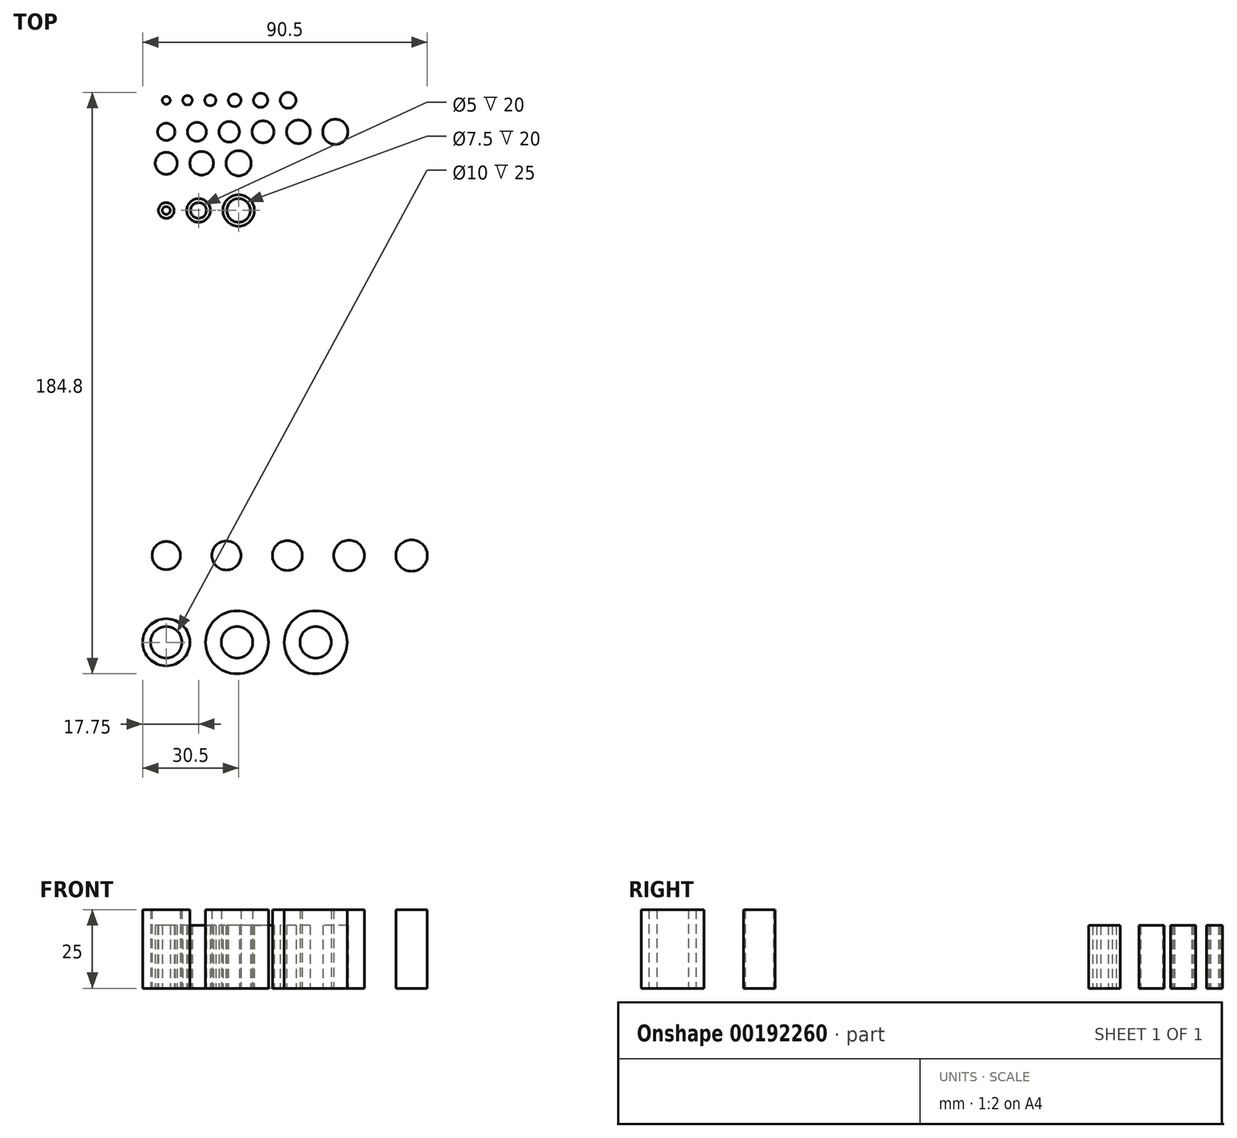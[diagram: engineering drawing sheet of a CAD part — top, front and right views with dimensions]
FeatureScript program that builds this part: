
annotation { "Feature Type Name" : "Feature", "Feature Type Description" : "" }
export const myFeature = defineFeature(function(context is Context, id is Id, definition is map)
    precondition{}
    {
        {
            var Q0;
            Q0=qCreatedBy(makeId("Top.planeOp"),FACE);
            var sketch = newSketch(context, id + "F0", { "sketchPlane" : qUnion([Q0])});
            skCircle(sketch, "E0", {"center": v(0, 0) * mm, "radius": 1.25 * mm});
            skCircle(sketch, "E1", {"center": v(38.75, 0) * mm, "radius": 2.5 * mm});
            skCircle(sketch, "E2", {"center": v(0, -35) * mm, "radius": 2.5 * mm});
            skCircle(sketch, "E3", {"center": v(10.25, -35) * mm, "radius": 3.75 * mm});
            skCircle(sketch, "E4", {"center": v(23, -35) * mm, "radius": 5 * mm});
            skCircle(sketch, "E5", {"center": v(0, -35) * mm, "radius": 1.25 * mm});
            skCircle(sketch, "E6", {"center": v(10.25, -35) * mm, "radius": 2.5 * mm});
            skCircle(sketch, "E7", {"center": v(23, -35) * mm, "radius": 3.75 * mm});
            skLineSegment(sketch, "E8", {"start": v(0, -35) * mm, "end": v(0, 0) * mm, "construction": true});
            skLineSegment(sketch, "E9", {"start": v(0, -35) * mm, "end": v(23, -35) * mm, "construction": true});
            skCircle(sketch, "E10", {"center": v(6.75, 0) * mm, "radius": 1.5 * mm});
            skCircle(sketch, "E11", {"center": v(14, 0) * mm, "radius": 1.75 * mm});
            skCircle(sketch, "E12", {"center": v(21.75, 0) * mm, "radius": 2 * mm});
            skCircle(sketch, "E13", {"center": v(30, 0) * mm, "radius": 2.25 * mm});
            skCircle(sketch, "E14", {"center": v(0, -10) * mm, "radius": 2.75 * mm});
            skCircle(sketch, "E15", {"center": v(9.75, -10) * mm, "radius": 3 * mm});
            skCircle(sketch, "E16", {"center": v(20, -10) * mm, "radius": 3.25 * mm});
            skCircle(sketch, "E17", {"center": v(30.75, -10) * mm, "radius": 3.5 * mm});
            skCircle(sketch, "E18", {"center": v(42, -10) * mm, "radius": 3.75 * mm});
            skCircle(sketch, "E19", {"center": v(53.75, -10) * mm, "radius": 4 * mm});
            skLineSegment(sketch, "E20", {"start": v(0, -10) * mm, "end": v(53.75, -10) * mm, "construction": true});
            skLineSegment(sketch, "E21", {"start": v(0, 0) * mm, "end": v(38.75, 0) * mm, "construction": true});
            skLineSegment(sketch, "E22", {"start": v(0, -20) * mm, "end": v(23, -20) * mm, "construction": true});
            skCircle(sketch, "E23", {"center": v(0, -20) * mm, "radius": 3.5 * mm});
            skCircle(sketch, "E24", {"center": v(11.25, -20) * mm, "radius": 3.75 * mm});
            skCircle(sketch, "E25", {"center": v(23, -20) * mm, "radius": 4 * mm});
            skSolve(sketch);
        }
        {
            var Q0;
            Q0=makeQuery(id+"F0.imprint","IMPRINT",FACE,{"disambiguationData":[TD([[makeQuery(id+"F0.imprint","IMPRINT",EDGE,{"derivedFrom":sQuery(id+"F0.wireOp",EDGE,"E0")}),1.0]])]});
            var Q1;
            Q1=makeQuery(id+"F0.imprint","IMPRINT",FACE,{"disambiguationData":[TD([[makeQuery(id+"F0.imprint","IMPRINT",EDGE,{"derivedFrom":sQuery(id+"F0.wireOp",EDGE,"E10")}),1.0]])]});
            var Q2;
            Q2=makeQuery(id+"F0.imprint","IMPRINT",FACE,{"disambiguationData":[TD([[makeQuery(id+"F0.imprint","IMPRINT",EDGE,{"derivedFrom":sQuery(id+"F0.wireOp",EDGE,"E11")}),1.0]])]});
            var Q3;
            Q3=makeQuery(id+"F0.imprint","IMPRINT",FACE,{"disambiguationData":[TD([[makeQuery(id+"F0.imprint","IMPRINT",EDGE,{"derivedFrom":sQuery(id+"F0.wireOp",EDGE,"E12")}),1.0]])]});
            var Q4;
            Q4=makeQuery(id+"F0.imprint","IMPRINT",FACE,{"disambiguationData":[TD([[makeQuery(id+"F0.imprint","IMPRINT",EDGE,{"derivedFrom":sQuery(id+"F0.wireOp",EDGE,"E13")}),1.0]])]});
            var Q5;
            Q5=makeQuery(id+"F0.imprint","IMPRINT",FACE,{"disambiguationData":[TD([[makeQuery(id+"F0.imprint","IMPRINT",EDGE,{"derivedFrom":sQuery(id+"F0.wireOp",EDGE,"E1")}),1.0]])]});
            var Q6;
            Q6=makeQuery(id+"F0.imprint","IMPRINT",FACE,{"disambiguationData":[TD([[makeQuery(id+"F0.imprint","IMPRINT",EDGE,{"derivedFrom":sQuery(id+"F0.wireOp",EDGE,"E14")}),1.0]])]});
            var Q7;
            Q7=makeQuery(id+"F0.imprint","IMPRINT",FACE,{"disambiguationData":[TD([[makeQuery(id+"F0.imprint","IMPRINT",EDGE,{"derivedFrom":sQuery(id+"F0.wireOp",EDGE,"E15")}),1.0]])]});
            var Q8;
            Q8=makeQuery(id+"F0.imprint","IMPRINT",FACE,{"disambiguationData":[TD([[makeQuery(id+"F0.imprint","IMPRINT",EDGE,{"derivedFrom":sQuery(id+"F0.wireOp",EDGE,"E16")}),1.0]])]});
            var Q9;
            Q9=makeQuery(id+"F0.imprint","IMPRINT",FACE,{"disambiguationData":[TD([[makeQuery(id+"F0.imprint","IMPRINT",EDGE,{"derivedFrom":sQuery(id+"F0.wireOp",EDGE,"E17")}),1.0]])]});
            var Q10;
            Q10=makeQuery(id+"F0.imprint","IMPRINT",FACE,{"disambiguationData":[TD([[makeQuery(id+"F0.imprint","IMPRINT",EDGE,{"derivedFrom":sQuery(id+"F0.wireOp",EDGE,"E18")}),1.0]])]});
            var Q11;
            Q11=makeQuery(id+"F0.imprint","IMPRINT",FACE,{"disambiguationData":[TD([[makeQuery(id+"F0.imprint","IMPRINT",EDGE,{"derivedFrom":sQuery(id+"F0.wireOp",EDGE,"E19")}),1.0]])]});
            var Q12;
            Q12=makeQuery(id+"F0.imprint","IMPRINT",FACE,{"disambiguationData":[TD([[makeQuery(id+"F0.imprint","IMPRINT",EDGE,{"derivedFrom":sQuery(id+"F0.wireOp",EDGE,"E25")}),1.0]])]});
            var Q13;
            {var subQ0=sQuery(id+"F0.wireOp",EDGE,"E24");var subQ1=sQuery(id+"F0.wireOp",EDGE,"E22");var subQ2=makeQuery(id+"F0.imprint","INTERSECT",VERTEX,{"disambiguationData":[OD(0.0)],"derivedFrom":[subQ1,subQ0]});Q13=makeQuery(id+"F0.imprint","IMPRINT",FACE,{"disambiguationData":[TD([[makeQuery(id+"F0.imprint","IMPRINT",EDGE,{"disambiguationData":[TD([[subQ2,-1.0]])],"derivedFrom":subQ1}),1.0]])]});}
            var Q14;
            Q14=makeQuery(id+"F0.imprint","IMPRINT",FACE,{"disambiguationData":[TD([[makeQuery(id+"F0.imprint","IMPRINT",EDGE,{"derivedFrom":sQuery(id+"F0.wireOp",EDGE,"E23")}),1.0]])]});
            var Q15;
            Q15=makeQuery(id+"F0.imprint","IMPRINT",FACE,{"disambiguationData":[TD([[makeQuery(id+"F0.imprint","IMPRINT",EDGE,{"derivedFrom":sQuery(id+"F0.wireOp",EDGE,"E2")}),1.0]])]});
            var Q16;
            Q16=makeQuery(id+"F0.imprint","IMPRINT",FACE,{"disambiguationData":[TD([[makeQuery(id+"F0.imprint","IMPRINT",EDGE,{"derivedFrom":sQuery(id+"F0.wireOp",EDGE,"E3")}),1.0]])]});
            var Q17;
            Q17=makeQuery(id+"F0.imprint","IMPRINT",FACE,{"disambiguationData":[TD([[makeQuery(id+"F0.imprint","IMPRINT",EDGE,{"derivedFrom":sQuery(id+"F0.wireOp",EDGE,"E4")}),1.0]])]});
            var Q18;
            Q18=makeQuery(id+"F0.imprint","IMPRINT",FACE,{"disambiguationData":[TD([[makeQuery(id+"F0.imprint","IMPRINT",EDGE,{"derivedFrom":sQuery(id+"F0.wireOp",EDGE,"E24")}),1.0]])]});
            extrude(context, id + "F1", {"entities" : qUnion([Q0, Q1, Q2, Q3, Q4, Q5, Q6, Q7, Q8, Q9, Q10, Q11, Q12, Q13, Q14, Q15, Q16, Q17, Q18]), "depth" : 20 * mm});
        }
        {
            var Q0;
            Q0=qCreatedBy(makeId("Top.planeOp"),FACE);
            var sketch = newSketch(context, id + "F2", { "sketchPlane" : qUnion([Q0])});
            skCircle(sketch, "E26", {"center": v(0, -172.3) * mm, "radius": 7.5 * mm});
            skCircle(sketch, "E27", {"center": v(22.5, -172.3) * mm, "radius": 10 * mm});
            skCircle(sketch, "E28", {"center": v(47.5, -172.3) * mm, "radius": 10 * mm});
            skCircle(sketch, "E29", {"center": v(22.5, -172.3) * mm, "radius": 5 * mm});
            skCircle(sketch, "E30", {"center": v(0, -172.3) * mm, "radius": 5 * mm});
            skCircle(sketch, "E31", {"center": v(47.5, -172.3) * mm, "radius": 5 * mm});
            skCircle(sketch, "E32", {"center": v(0, -144.72) * mm, "radius": 4.5 * mm});
            skCircle(sketch, "E33", {"center": v(19.12, -144.72) * mm, "radius": 4.62 * mm});
            skCircle(sketch, "E34", {"center": v(38.5, -144.72) * mm, "radius": 4.75 * mm});
            skCircle(sketch, "E35", {"center": v(58.12, -144.72) * mm, "radius": 4.88 * mm});
            skCircle(sketch, "E36", {"center": v(78, -144.72) * mm, "radius": 5 * mm});
            skSolve(sketch);
        }
        {
            var Q0;
            Q0 = qSketchRegion(id + "F2", true);
            extrude(context, id + "F3", {"entities" : qUnion([Q0]), "depth" : 25 * mm});
        }
    });
